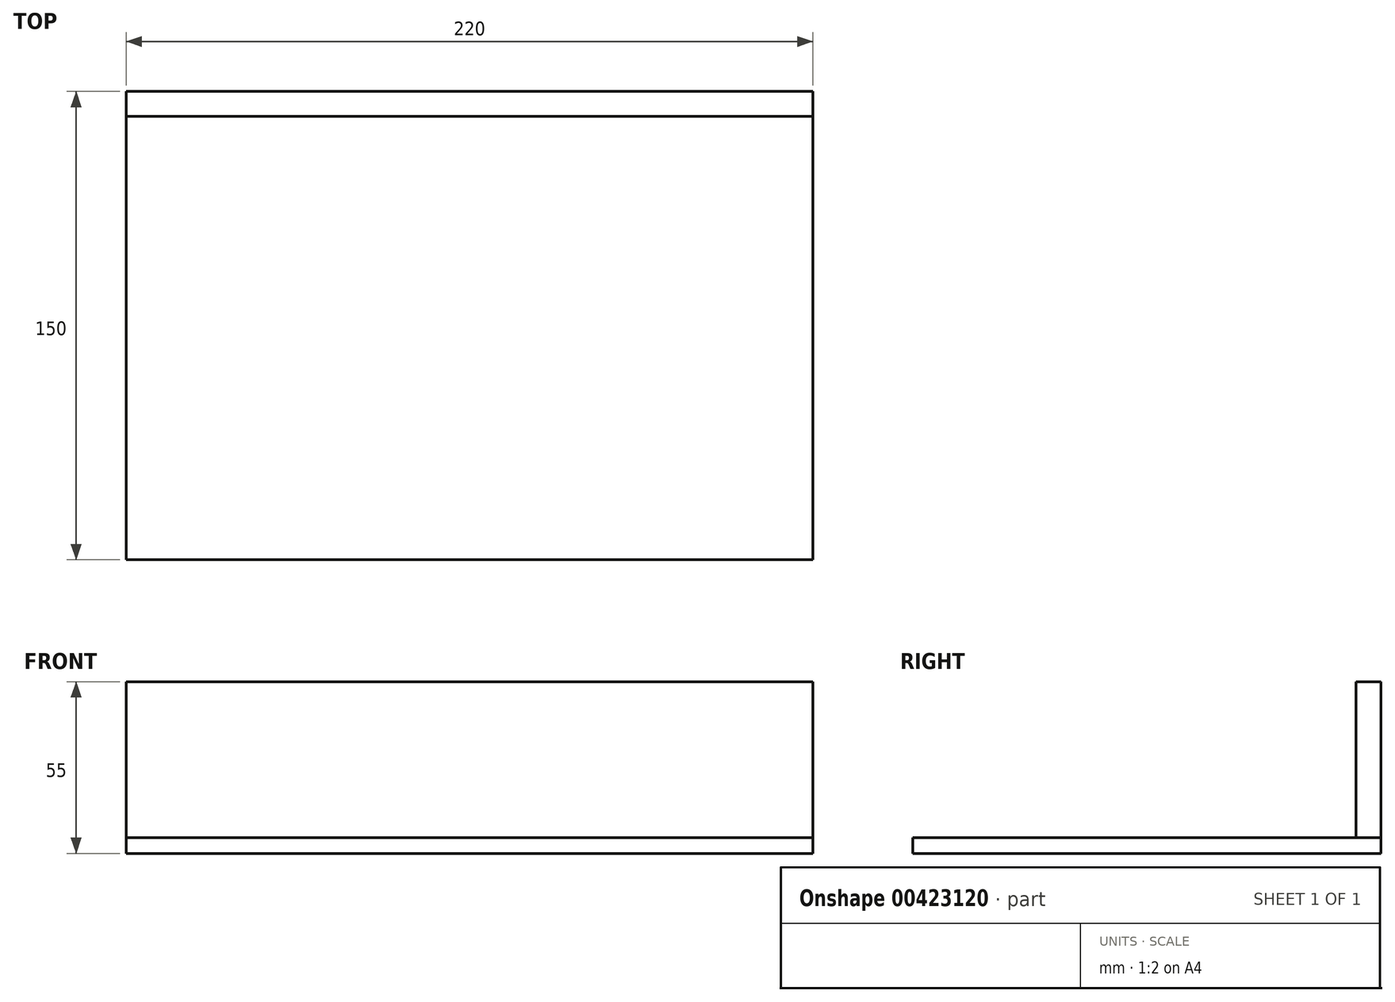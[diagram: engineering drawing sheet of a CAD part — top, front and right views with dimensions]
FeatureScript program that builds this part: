
annotation { "Feature Type Name" : "Feature", "Feature Type Description" : "" }
export const myFeature = defineFeature(function(context is Context, id is Id, definition is map)
    precondition{}
    {
        {
            var Q0;
            Q0=qCreatedBy(makeId("Top.planeOp"),FACE);
            var sketch = newSketch(context, id + "F0", { "sketchPlane" : qUnion([Q0])});
            skLineSegment(sketch, "E0.bottom", {"start": v(110, 75) * mm, "end": v(-110, 75) * mm});
            skLineSegment(sketch, "E0.top", {"start": v(110, -75) * mm, "end": v(-110, -75) * mm});
            skLineSegment(sketch, "E0.left", {"start": v(110, 75) * mm, "end": v(110, -75) * mm});
            skLineSegment(sketch, "E0.right", {"start": v(-110, 75) * mm, "end": v(-110, -75) * mm});
            skPoint(sketch, "E0.middle", {"position": v(0, 0) * mm});
            skSolve(sketch);
        }
        {
            var Q0;
            Q0 = qSketchRegion(id + "F0", true);
            extrude(context, id + "F1", {"entities" : qUnion([Q0]), "depth" : 5 * mm});
        }
        {
            var Q0;
            Q0=makeQuery(id+"F1.opExtrude","CAP_FACE",FACE,{"disambiguationData":[OSD([sQuery(id+"F0.wireOp",EDGE,"E0.bottom"),sQuery(id+"F0.wireOp",EDGE,"E0.top"),sQuery(id+"F0.wireOp",EDGE,"E0.left"),sQuery(id+"F0.wireOp",EDGE,"E0.right")])],"isStart":false});
            var sketch = newSketch(context, id + "F2", { "sketchPlane" : qUnion([Q0])});
            skLineSegment(sketch, "E1.0", {"start": v(110, 75) * mm, "end": v(-110, 75) * mm});
            skLineSegment(sketch, "E2.0", {"start": v(110, 67) * mm, "end": v(-110, 67) * mm});
            skLineSegment(sketch, "E3", {"start": v(-110, 75) * mm, "end": v(-110, 67) * mm});
            skLineSegment(sketch, "E4", {"start": v(110, 75) * mm, "end": v(110, 67) * mm});
            skSolve(sketch);
        }
        {
            var Q0;
            Q0=makeQuery(id+"F2.imprint","IMPRINT",FACE,{"disambiguationData":[TD([[makeQuery(id+"F2.imprint","IMPRINT",EDGE,{"derivedFrom":sQuery(id+"F2.wireOp",EDGE,"E1.0")}),1.0]])]});
            extrude(context, id + "F3", {"entities" : qUnion([Q0]), "depth" : 50 * mm});
        }
    });
